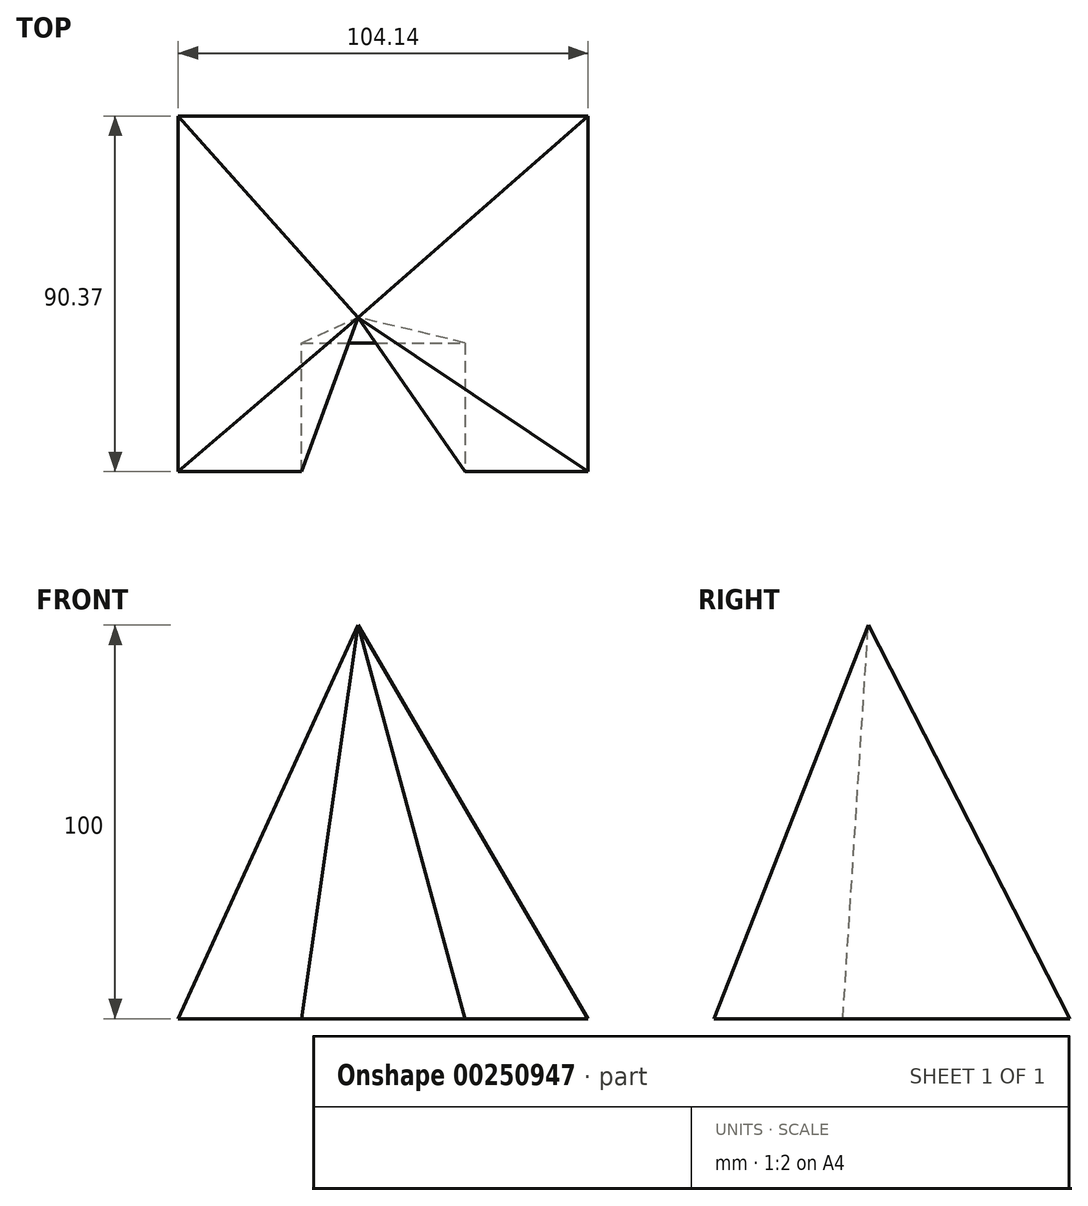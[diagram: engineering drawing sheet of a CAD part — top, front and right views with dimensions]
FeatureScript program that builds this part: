
annotation { "Feature Type Name" : "Feature", "Feature Type Description" : "" }
export const myFeature = defineFeature(function(context is Context, id is Id, definition is map)
    precondition{}
    {
        {
            var Q0;
            Q0=qCreatedBy(makeId("Top.planeOp"),FACE);
            var sketch = newSketch(context, id + "F0", { "sketchPlane" : qUnion([Q0])});
            skLineSegment(sketch, "E0", {"start": v(-55.08, 39.16) * mm, "end": v(-55.08, -51.2) * mm});
            skLineSegment(sketch, "E1", {"start": v(-55.08, -51.2) * mm, "end": v(-23.81, -51.2) * mm});
            skLineSegment(sketch, "E2", {"start": v(-23.81, -51.2) * mm, "end": v(-23.81, -18.5) * mm});
            skLineSegment(sketch, "E3", {"start": v(-23.81, -18.5) * mm, "end": v(17.79, -18.5) * mm});
            skLineSegment(sketch, "E4", {"start": v(17.79, -18.5) * mm, "end": v(17.79, -51.2) * mm});
            skLineSegment(sketch, "E5", {"start": v(17.79, -51.2) * mm, "end": v(49.06, -51.2) * mm});
            skLineSegment(sketch, "E6", {"start": v(49.06, -51.2) * mm, "end": v(49.06, 40.02) * mm});
            skLineSegment(sketch, "E7", {"start": v(-55.08, 39.16) * mm, "end": v(49.06, 39.16) * mm});
            skPoint(sketch, "E8", {"position": v(0, 0) * mm});
            skSolve(sketch);
        }
        {
            var Q0;
            Q0=qCreatedBy(makeId("Top.planeOp"),FACE);
            cPlane(context, id + "F1", {"entities" : qUnion([Q0]), "cplaneType" : CPlaneType.OFFSET, "offset" : 100 * mm, "width" : 150 * mm, "height" : 150 * mm});
        }
        {
            var Q0;
            Q0=qCreatedBy(id+"F1.planeOp",FACE);
            var sketch = newSketch(context, id + "F2", { "sketchPlane" : qUnion([Q0])});
            skPoint(sketch, "E9", {"position": v(-9.38, -12.05) * mm});
            skSolve(sketch);
        }
        {
            var Q0;
            Q0=makeQuery(id+"F0.imprint","IMPRINT",FACE,{"disambiguationData":[TD([[makeQuery(id+"F0.imprint","IMPRINT",EDGE,{"derivedFrom":sQuery(id+"F0.wireOp",EDGE,"E0")}),1.0]])]});
            var Q1;
            Q1=sQuery(id+"F2.wireOp",VERTEX,"E9");
            loft(context, id + "F3", {"sheetProfilesArray" : [{ "sheetProfileEntities" : qUnion([Q0]) }, { "sheetProfileEntities" : qUnion([Q1]) }]});
        }
    });
